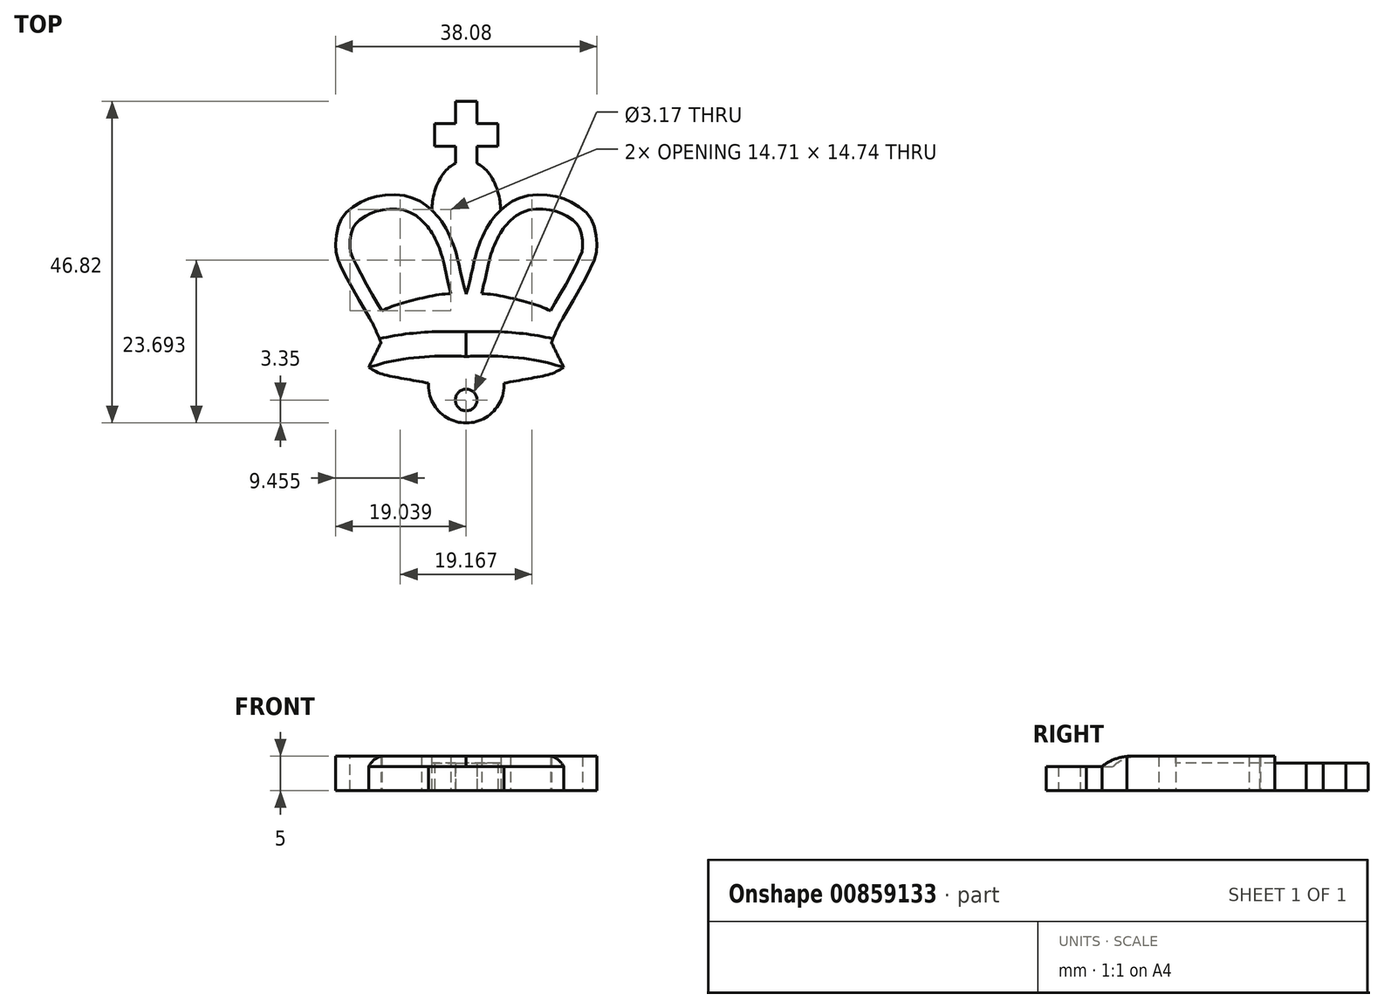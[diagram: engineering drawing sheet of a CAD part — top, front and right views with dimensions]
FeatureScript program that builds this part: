
annotation { "Feature Type Name" : "Feature", "Feature Type Description" : "" }
export const myFeature = defineFeature(function(context is Context, id is Id, definition is map)
    precondition{}
    {
        {
            var Q0;
            Q0=qCreatedBy(makeId("Top.planeOp"),FACE);
            var sketch = newSketch(context, id + "F0", { "sketchPlane" : qUnion([Q0])});
            skLineSegment(sketch, "E0", {"start": v(-5.48, 27.72) * mm, "end": v(-7.02, 27.72) * mm});
            skLineSegment(sketch, "E1", {"start": v(-7.02, 27.72) * mm, "end": v(-7.02, 24.48) * mm});
            skLineSegment(sketch, "E2", {"start": v(-7.02, 24.48) * mm, "end": v(-10.07, 24.48) * mm});
            skLineSegment(sketch, "E3", {"start": v(-10.07, 24.48) * mm, "end": v(-10.07, 21.2) * mm});
            skLineSegment(sketch, "E4", {"start": v(-10.07, 21.2) * mm, "end": v(-7.02, 21.2) * mm});
            skLineSegment(sketch, "E5", {"start": v(-7.02, 21.2) * mm, "end": v(-7.02, 18.72) * mm});
            skFitSpline(sketch, "E6", {"points": [v(-7.02, 18.72) * mm, v(-8.13, 17.96) * mm, v(-9.43, 16.23) * mm, v(-10.3, 13.7) * mm, v(-10.5, 11.92) * mm], "startDerivative": vector(-5.39, -3.12) * mm, "endDerivative": vector(-0.53, -7.06) * mm});
            skFitSpline(sketch, "E7", {"points": [v(-10.5, 11.92) * mm, v(-12.07, 13.1) * mm, v(-14.66, 14.02) * mm, v(-18.17, 13.97) * mm, v(-20.65, 13.1) * mm, v(-23.18, 11.27) * mm, v(-24.26, 8.95) * mm, v(-24.48, 5.98) * mm, v(-23.56, 3.4) * mm, v(-20.86, -1.62) * mm, v(-19.03, -4.8) * mm, v(-17.9, -7.4) * mm], "startDerivative": vector(-19.92, 17.16) * mm, "endDerivative": vector(12, -29.86) * mm});
            skFitSpline(sketch, "E8", {"points": [v(-17.9, -7.4) * mm, v(-19.68, -11.01) * mm], "startDerivative": vector(-1.78, -3.61) * mm, "endDerivative": vector(-1.78, -3.61) * mm});
            skFitSpline(sketch, "E9", {"points": [v(-19.68, -11.01) * mm, v(-17.9, -11.93) * mm, v(-14.66, -12.63) * mm, v(-10.5, -13.33) * mm, v(-7.02, -13.55) * mm, v(-5.48, -13.6) * mm], "startDerivative": vector(9.65, -5.97) * mm, "endDerivative": vector(9.37, -0.34) * mm});
            skFitSpline(sketch, "E10", {"points": [v(-10.5, 11.92) * mm, v(-8.96, 10.08) * mm, v(-7.43, 7.07) * mm, v(-6.63, 4.36) * mm, v(-5.87, 1) * mm, v(-5.48, -0.33) * mm], "startDerivative": vector(8.24, -8.6) * mm, "endDerivative": vector(2.53, -7.9) * mm});
            skFitSpline(sketch, "E11", {"points": [v(-5.48, -0.33) * mm, v(-8.63, -0.33) * mm, v(-13.44, -1.3) * mm, v(-17.2, -2.52) * mm, v(-19.56, -3.84) * mm], "startDerivative": vector(-12.72, 0.73) * mm, "endDerivative": vector(-10.25, -6.5) * mm});
            skFitSpline(sketch, "E12", {"points": [v(-5.48, -4.92) * mm, v(-9.22, -5.24) * mm, v(-13.17, -5.92) * mm, v(-16.66, -7) * mm, v(-17.9, -7.4) * mm], "startDerivative": vector(-13.46, -0.97) * mm, "endDerivative": vector(-6.6, -2) * mm});
            skFitSpline(sketch, "E13", {"points": [v(-19.68, -11.01) * mm, v(-16.02, -10.05) * mm, v(-10.54, -9.41) * mm, v(-6.86, -9.37) * mm, v(-5.48, -9.41) * mm], "startDerivative": vector(12.95, 3.95) * mm, "endDerivative": vector(7.75, -0.31) * mm});
            skLineSegment(sketch, "E14.MirrorCS", {"start": v(-5.48, 27.72) * mm, "end": v(-3.94, 27.72) * mm});
            skLineSegment(sketch, "E15.MirrorCS", {"start": v(-3.94, 27.72) * mm, "end": v(-3.94, 24.48) * mm});
            skLineSegment(sketch, "E16.MirrorCS", {"start": v(-3.94, 24.48) * mm, "end": v(-0.89, 24.48) * mm});
            skLineSegment(sketch, "E17.MirrorCS", {"start": v(-0.89, 24.48) * mm, "end": v(-0.89, 21.2) * mm});
            skLineSegment(sketch, "E18.MirrorCS", {"start": v(-0.89, 21.2) * mm, "end": v(-3.94, 21.2) * mm});
            skLineSegment(sketch, "E19.MirrorCS", {"start": v(-3.94, 21.2) * mm, "end": v(-3.94, 18.72) * mm});
            skFitSpline(sketch, "E20.MirrorCS", {"points": [v(-3.94, 18.72) * mm, v(-2.83, 17.96) * mm, v(-1.54, 16.23) * mm, v(-0.67, 13.7) * mm, v(-0.46, 11.92) * mm], "startDerivative": vector(5.39, -3.12) * mm, "endDerivative": vector(0.53, -7.06) * mm});
            skFitSpline(sketch, "E21.MirrorCS", {"points": [v(-0.46, 11.92) * mm, v(1.1, 13.1) * mm, v(3.7, 14.02) * mm, v(7.2, 13.97) * mm, v(9.69, 13.1) * mm, v(12.22, 11.27) * mm, v(13.3, 8.95) * mm, v(13.52, 5.98) * mm, v(12.6, 3.4) * mm, v(9.9, -1.62) * mm, v(8.07, -4.8) * mm, v(6.93, -7.4) * mm], "startDerivative": vector(19.92, 17.16) * mm, "endDerivative": vector(-12, -29.86) * mm});
            skFitSpline(sketch, "E22.MirrorCS", {"points": [v(-0.46, 11.92) * mm, v(-2, 10.08) * mm, v(-3.53, 7.07) * mm, v(-4.33, 4.36) * mm, v(-5.1, 1) * mm, v(-5.48, -0.33) * mm], "startDerivative": vector(-8.24, -8.6) * mm, "endDerivative": vector(-2.53, -7.9) * mm});
            skFitSpline(sketch, "E23.MirrorCS", {"points": [v(-5.48, -0.33) * mm, v(-2.33, -0.33) * mm, v(2.48, -1.3) * mm, v(6.24, -2.52) * mm, v(8.6, -3.84) * mm], "startDerivative": vector(12.72, 0.73) * mm, "endDerivative": vector(10.25, -6.5) * mm});
            skFitSpline(sketch, "E24.MirrorCS", {"points": [v(-5.48, -4.92) * mm, v(-1.74, -5.24) * mm, v(2.2, -5.92) * mm, v(5.7, -7) * mm, v(6.93, -7.4) * mm], "startDerivative": vector(13.46, -0.97) * mm, "endDerivative": vector(6.6, -2) * mm});
            skFitSpline(sketch, "E25.MirrorCS", {"points": [v(8.71, -11.01) * mm, v(5.06, -10.05) * mm, v(-0.43, -9.41) * mm, v(-4.1, -9.37) * mm, v(-5.48, -9.41) * mm], "startDerivative": vector(-12.95, 3.95) * mm, "endDerivative": vector(-7.75, -0.31) * mm});
            skFitSpline(sketch, "E26.MirrorCS", {"points": [v(6.93, -7.4) * mm, v(8.71, -11.01) * mm], "startDerivative": vector(1.78, -3.61) * mm, "endDerivative": vector(1.78, -3.61) * mm});
            skFitSpline(sketch, "E27.MirrorCS", {"points": [v(8.71, -11.01) * mm, v(6.93, -11.93) * mm, v(3.7, -12.63) * mm, v(-0.46, -13.33) * mm, v(-3.94, -13.55) * mm, v(-5.48, -13.6) * mm], "startDerivative": vector(-9.65, -5.97) * mm, "endDerivative": vector(-9.37, -0.34) * mm});
            skArc(sketch, "E28", {"start": v(-10.97, -13.27) * mm, "mid": v(-5.48, -19.1) * mm, "end": v(0, -13.27) * mm});
            skCircle(sketch, "E29", {"center": v(-5.48, -15.75) * mm, "radius": 1.59 * mm});
            skFitSpline(sketch, "E30.0", {"points": [v(-11.88, 10.33) * mm, v(-12.08, 10.5) * mm, v(-12.46, 10.83) * mm, v(-12.89, 11.14) * mm, v(-13.23, 11.35) * mm, v(-13.61, 11.55) * mm, v(-14.05, 11.72) * mm, v(-14.54, 11.86) * mm, v(-14.93, 11.94) * mm, v(-15.34, 12) * mm, v(-15.8, 12.03) * mm, v(-16.28, 12.04) * mm, v(-16.75, 12.02) * mm, v(-17.22, 11.99) * mm, v(-17.65, 11.93) * mm, v(-18.05, 11.85) * mm, v(-18.4, 11.77) * mm, v(-18.73, 11.66) * mm, v(-19.06, 11.53) * mm, v(-19.35, 11.4) * mm, v(-19.6, 11.28) * mm, v(-19.86, 11.15) * mm, v(-20.19, 10.97) * mm, v(-20.57, 10.74) * mm, v(-20.93, 10.5) * mm, v(-21.24, 10.25) * mm, v(-21.45, 10.05) * mm, v(-21.58, 9.91) * mm, v(-21.69, 9.79) * mm, v(-21.8, 9.62) * mm, v(-21.92, 9.4) * mm, v(-22.03, 9.15) * mm, v(-22.11, 8.89) * mm, v(-22.18, 8.65) * mm, v(-22.24, 8.39) * mm, v(-22.34, 7.9) * mm, v(-22.4, 7.32) * mm, v(-22.43, 6.79) * mm, v(-22.42, 6.49) * mm, v(-22.4, 6.28) * mm, v(-22.37, 6.1) * mm, v(-22.33, 5.87) * mm, v(-22.25, 5.6) * mm, v(-22.12, 5.27) * mm, v(-21.95, 4.88) * mm, v(-21.72, 4.41) * mm, v(-21.45, 3.86) * mm, v(-21.04, 3.07) * mm, v(-20.48, 2) * mm, v(-19.76, 0.68) * mm, v(-19.17, -0.36) * mm, v(-18.74, -1.1) * mm, v(-18.32, -1.8) * mm, v(-17.92, -2.46) * mm, v(-17.55, -3.13) * mm, v(-17.27, -3.63) * mm, v(-17, -4.15) * mm, v(-16.69, -4.83) * mm, v(-16.33, -5.66) * mm, v(-16.07, -6.3) * mm, v(-15.95, -6.61) * mm]});
            skFitSpline(sketch, "E30.1", {"points": [v(-12.02, 10.46) * mm, v(-11.85, 10.28) * mm, v(-11.53, 9.95) * mm, v(-11.18, 9.55) * mm, v(-10.91, 9.21) * mm, v(-10.72, 8.95) * mm, v(-10.53, 8.65) * mm, v(-10.27, 8.21) * mm, v(-9.95, 7.6) * mm, v(-9.65, 6.95) * mm, v(-9.44, 6.45) * mm, v(-9.26, 5.97) * mm, v(-9.07, 5.4) * mm, v(-8.88, 4.71) * mm, v(-8.68, 3.92) * mm, v(-8.47, 2.98) * mm, v(-8.26, 1.99) * mm, v(-8.04, 1.04) * mm, v(-7.77, -0.07) * mm, v(-7.59, -0.64) * mm, v(-7.48, -0.97) * mm]});
            skFitSpline(sketch, "E31.0", {"points": [v(0.91, 10.33) * mm, v(1.12, 10.5) * mm, v(1.5, 10.83) * mm, v(1.92, 11.14) * mm, v(2.27, 11.35) * mm, v(2.65, 11.55) * mm, v(3.09, 11.72) * mm, v(3.57, 11.86) * mm, v(3.96, 11.94) * mm, v(4.38, 12) * mm, v(4.84, 12.03) * mm, v(5.31, 12.04) * mm, v(5.8, 12.02) * mm, v(6.25, 11.99) * mm, v(6.7, 11.93) * mm, v(7.08, 11.85) * mm, v(7.43, 11.77) * mm, v(7.76, 11.66) * mm, v(8.1, 11.53) * mm, v(8.39, 11.4) * mm, v(8.63, 11.28) * mm, v(8.9, 11.15) * mm, v(9.22, 10.97) * mm, v(9.6, 10.74) * mm, v(9.96, 10.5) * mm, v(10.28, 10.25) * mm, v(10.49, 10.05) * mm, v(10.62, 9.91) * mm, v(10.72, 9.79) * mm, v(10.84, 9.62) * mm, v(10.96, 9.4) * mm, v(11.07, 9.15) * mm, v(11.15, 8.89) * mm, v(11.21, 8.65) * mm, v(11.28, 8.39) * mm, v(11.37, 7.9) * mm, v(11.44, 7.32) * mm, v(11.46, 6.79) * mm, v(11.46, 6.49) * mm, v(11.44, 6.28) * mm, v(11.41, 6.1) * mm, v(11.37, 5.87) * mm, v(11.28, 5.6) * mm, v(11.16, 5.27) * mm, v(10.99, 4.88) * mm, v(10.76, 4.41) * mm, v(10.49, 3.86) * mm, v(10.08, 3.07) * mm, v(9.51, 2) * mm, v(8.8, 0.68) * mm, v(8.2, -0.36) * mm, v(7.78, -1.1) * mm, v(7.36, -1.8) * mm, v(6.96, -2.46) * mm, v(6.58, -3.13) * mm, v(6.3, -3.63) * mm, v(6.04, -4.15) * mm, v(5.72, -4.83) * mm, v(5.37, -5.66) * mm, v(5.11, -6.3) * mm, v(4.99, -6.61) * mm]});
            skFitSpline(sketch, "E31.1", {"points": [v(1.06, 10.46) * mm, v(0.89, 10.28) * mm, v(0.57, 9.95) * mm, v(0.21, 9.55) * mm, v(-0.05, 9.21) * mm, v(-0.24, 8.95) * mm, v(-0.43, 8.65) * mm, v(-0.7, 8.21) * mm, v(-1.02, 7.6) * mm, v(-1.31, 6.95) * mm, v(-1.52, 6.45) * mm, v(-1.7, 5.97) * mm, v(-1.9, 5.4) * mm, v(-2.09, 4.71) * mm, v(-2.28, 3.92) * mm, v(-2.5, 2.98) * mm, v(-2.7, 1.99) * mm, v(-2.92, 1.04) * mm, v(-3.2, -0.07) * mm, v(-3.38, -0.64) * mm, v(-3.48, -0.97) * mm]});
            skSolve(sketch);
        }
        {
            var Q0;
            {var subQ4=sQuery(id+"F0.wireOp",EDGE,"E10");Q0=makeQuery(id+"F0.imprint","IMPRINT",FACE,{"disambiguationData":[TD([[makeQuery(id+"F0.imprint","IMPRINT",EDGE,{"derivedFrom":subQ4}),-1.0]])]});}
            var Q1;
            {var subQ1=sQuery(id+"F0.wireOp",EDGE,"E22.MirrorCS");Q1=makeQuery(id+"F0.imprint","IMPRINT",FACE,{"disambiguationData":[TD([[makeQuery(id+"F0.imprint","IMPRINT",EDGE,{"derivedFrom":subQ1}),1.0]])]});}
            var Q2;
            {var subQ10=sQuery(id+"F0.wireOp",EDGE,"E12");Q2=makeQuery(id+"F0.imprint","IMPRINT",FACE,{"disambiguationData":[TD([[makeQuery(id+"F0.imprint","IMPRINT",EDGE,{"derivedFrom":subQ10}),-1.0]])]});}
            extrude(context, id + "F1", {"entities" : qUnion([Q0, Q1, Q2]), "depth" : 5 * mm, "offsetDistance" : 25 * mm});
        }
        {
            var Q0;
            Q0=makeQuery(id+"F0.imprint","IMPRINT",FACE,{"disambiguationData":[TD([[makeQuery(id+"F0.imprint","IMPRINT",EDGE,{"derivedFrom":sQuery(id+"F0.wireOp",EDGE,"E0")}),1.0]])]});
            extrude(context, id + "F2", {"entities" : qUnion([Q0]), "operationType" : NewBodyOperationType.ADD, "depth" : 4 * mm, "offsetDistance" : 25 * mm});
        }
        {
            var Q0;
            Q0=makeQuery(id+"F0.imprint","IMPRINT",FACE,{"disambiguationData":[TD([[makeQuery(id+"F0.imprint","IMPRINT",EDGE,{"derivedFrom":sQuery(id+"F0.wireOp",EDGE,"E8")}),1.0]])]});
            extrude(context, id + "F3", {"entities" : qUnion([Q0]), "operationType" : NewBodyOperationType.ADD, "depth" : 5 * mm, "offsetDistance" : 25 * mm});
        }
        {
            var Q0;
            {var subQ1=sQuery(id+"F0.wireOp",EDGE,"E13");Q0=makeQuery(id+"F0.imprint","IMPRINT",FACE,{"disambiguationData":[TD([[makeQuery(id+"F0.imprint","IMPRINT",EDGE,{"derivedFrom":subQ1}),-1.0]])]});}
            var Q1;
            {var subQ3=sQuery(id+"F0.wireOp",EDGE,"E28");Q1=makeQuery(id+"F0.imprint","IMPRINT",FACE,{"disambiguationData":[TD([[makeQuery(id+"F0.imprint","IMPRINT",EDGE,{"derivedFrom":subQ3}),1.0]])]});}
            extrude(context, id + "F4", {"entities" : qUnion([Q0, Q1]), "operationType" : NewBodyOperationType.ADD, "depth" : 3.5 * mm, "offsetDistance" : 25 * mm});
        }
        {
            var Q0;
            Q0=makeQuery(id+"F3.opExtrude","CAP_EDGE",EDGE,{"disambiguationData":[OSD([sQuery(id+"F0.wireOp",EDGE,"E13")])],"isStart":false});
            var Q1;
            Q1=makeQuery(id+"F3.opExtrude","CAP_EDGE",EDGE,{"disambiguationData":[OSD([sQuery(id+"F0.wireOp",EDGE,"E25.MirrorCS")])],"isStart":false});
            fillet(context, id + "F5", {"entities" : qUnion([Q0, Q1]), "radius" : 5 * mm, "tangentPropagation" : true, "allowEdgeOverflow" : false});
        }
    });
